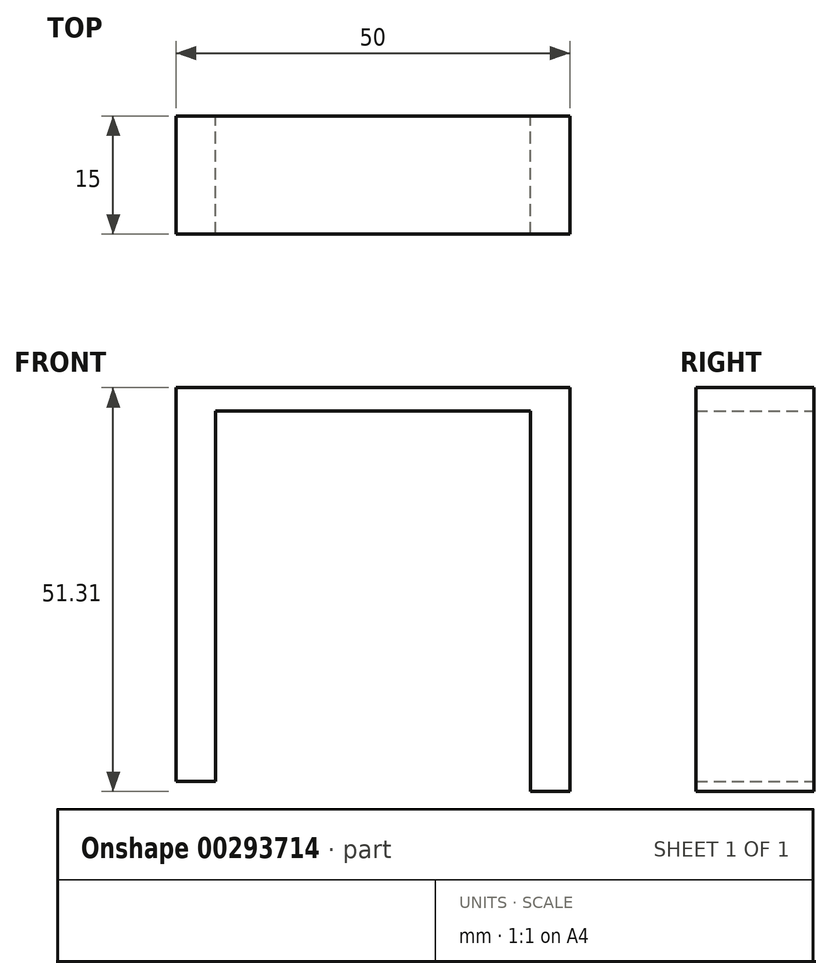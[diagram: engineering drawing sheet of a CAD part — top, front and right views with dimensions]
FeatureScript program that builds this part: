
annotation { "Feature Type Name" : "Feature", "Feature Type Description" : "" }
export const myFeature = defineFeature(function(context is Context, id is Id, definition is map)
    precondition{}
    {
        {
            var Q0;
            Q0=qCreatedBy(makeId("Front.planeOp"),FACE);
            var sketch = newSketch(context, id + "F0", { "sketchPlane" : qUnion([Q0])});
            skLineSegment(sketch, "E0", {"start": v(-21.92, -14.7) * mm, "end": v(-21.92, 35.3) * mm});
            skLineSegment(sketch, "E1", {"start": v(-21.92, 35.3) * mm, "end": v(28.08, 35.3) * mm});
            skLineSegment(sketch, "E2", {"start": v(28.08, 35.3) * mm, "end": v(28.08, -16.01) * mm});
            skLineSegment(sketch, "E3", {"start": v(28.08, -16.01) * mm, "end": v(23.08, -16.01) * mm});
            skLineSegment(sketch, "E4", {"start": v(23.08, -16.01) * mm, "end": v(23.08, 32.3) * mm});
            skLineSegment(sketch, "E5", {"start": v(23.08, 32.3) * mm, "end": v(-16.92, 32.3) * mm});
            skLineSegment(sketch, "E6", {"start": v(-16.92, 32.3) * mm, "end": v(-16.92, -14.7) * mm});
            skLineSegment(sketch, "E7", {"start": v(-16.92, -14.7) * mm, "end": v(-21.92, -14.7) * mm});
            skSolve(sketch);
        }
        {
            var Q0;
            Q0 = qSketchRegion(id + "F0", true);
            extrude(context, id + "F1", {"entities" : qUnion([Q0]), "depth" : 15 * mm});
        }
    });
